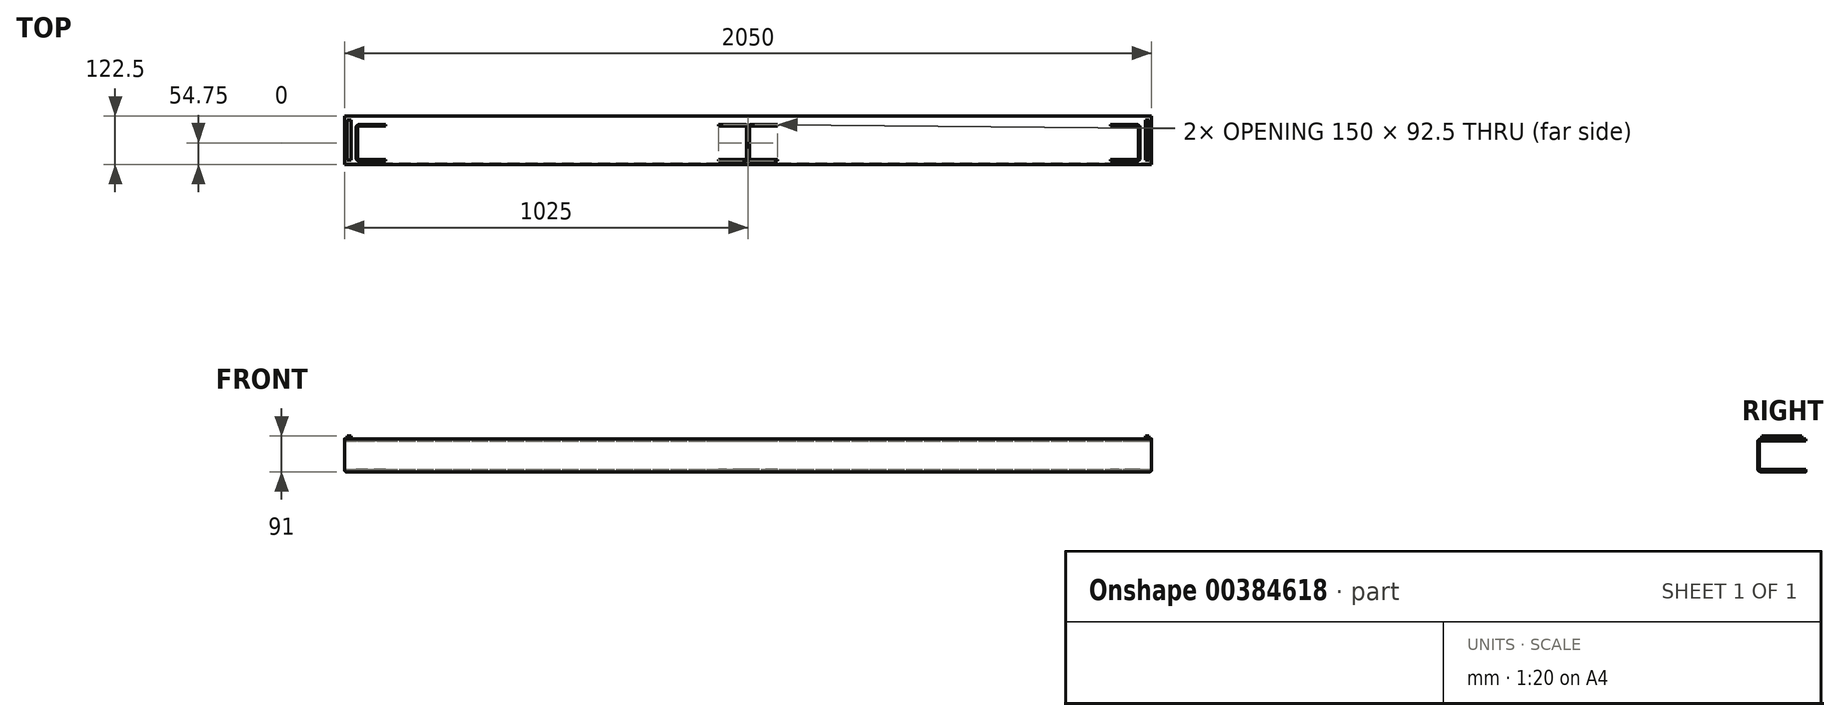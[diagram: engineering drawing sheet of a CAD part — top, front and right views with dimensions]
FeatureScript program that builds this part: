
annotation { "Feature Type Name" : "Feature", "Feature Type Description" : "" }
export const myFeature = defineFeature(function(context is Context, id is Id, definition is map)
    precondition{}
    {
        {
            var Q0;
            Q0=qCreatedBy(makeId("Right.planeOp"),FACE);
            var sketch = newSketch(context, id + "F0", { "sketchPlane" : qUnion([Q0])});
            skLineSegment(sketch, "E0.bottom", {"start": v(-45.5, -41.75) * mm, "end": v(0, -41.75) * mm});
            skLineSegment(sketch, "E0.top", {"start": v(-45.5, 41.75) * mm, "end": v(0, 41.75) * mm});
            skLineSegment(sketch, "E0.left", {"start": v(-53.5, -33.75) * mm, "end": v(-53.5, 33.75) * mm});
            skPoint(sketch, "E0.middle", {"position": v(0, 0) * mm});
            skLineSegment(sketch, "E1", {"start": v(0, 36) * mm, "end": v(-45.5, 36) * mm});
            skLineSegment(sketch, "E2", {"start": v(-49.5, 32) * mm, "end": v(-49.5, -32) * mm});
            skLineSegment(sketch, "E3", {"start": v(-45.5, -36) * mm, "end": v(0, -36) * mm});
            skPoint(sketch, "E4.visualSharp", {"position": v(-49.5, 36) * mm});
            skArc(sketch, "E4.filletArc", {"start": v(-45.5, 36) * mm, "mid": v(-48.33, 34.83) * mm, "end": v(-49.5, 32) * mm});
            skPoint(sketch, "E5.visualSharp", {"position": v(-49.5, -36) * mm});
            skArc(sketch, "E5.filletArc", {"start": v(-49.5, -32) * mm, "mid": v(-48.33, -34.83) * mm, "end": v(-45.5, -36) * mm});
            skPoint(sketch, "E6.visualSharp", {"position": v(-53.5, 41.75) * mm});
            skArc(sketch, "E6.filletArc", {"start": v(-45.5, 41.75) * mm, "mid": v(-51.16, 39.4) * mm, "end": v(-53.5, 33.75) * mm});
            skPoint(sketch, "E7.visualSharp", {"position": v(-53.5, -41.75) * mm});
            skArc(sketch, "E7.filletArc", {"start": v(-53.5, -33.75) * mm, "mid": v(-51.16, -39.4) * mm, "end": v(-45.5, -41.75) * mm});
            skLineSegment(sketch, "E8", {"start": v(0, 41.75) * mm, "end": v(0, -41.75) * mm});
            skPoint(sketch, "E8.startSnap0", {"position": v(4, 41.75) * mm});
            skPoint(sketch, "E9.start.orphan", {"position": v(53.5, 41.75) * mm});
            skPoint(sketch, "E0.right.start.orphan", {"position": v(53.5, -41.75) * mm});
            skLineSegment(sketch, "E10", {"start": v(0, 41.75) * mm, "end": v(69, 41.75) * mm});
            skLineSegment(sketch, "E11", {"start": v(69, 41.75) * mm, "end": v(69, 36) * mm});
            skLineSegment(sketch, "E12", {"start": v(0, -41.75) * mm, "end": v(69, -41.75) * mm});
            skLineSegment(sketch, "E13", {"start": v(69, -41.75) * mm, "end": v(69, -36) * mm});
            skLineSegment(sketch, "E14", {"start": v(69, -36) * mm, "end": v(0, -36) * mm});
            skLineSegment(sketch, "E15", {"start": v(69, 36) * mm, "end": v(0, 36) * mm});
            skSolve(sketch);
        }
        {
            var Q0;
            Q0=makeQuery(id+"F0.imprint","IMPRINT",FACE,{"disambiguationData":[TD([[makeQuery(id+"F0.imprint","IMPRINT",EDGE,{"derivedFrom":sQuery(id+"F0.wireOp",EDGE,"E0.bottom")}),1.0]])]});
            var Q1;
            {var subQ0=sQuery(id+"F0.wireOp",EDGE,"E10");Q1=makeQuery(id+"F0.imprint","IMPRINT",FACE,{"disambiguationData":[TD([[makeQuery(id+"F0.imprint","IMPRINT",EDGE,{"derivedFrom":subQ0}),-1.0]])]});}
            var Q2;
            {var subQ0=sQuery(id+"F0.wireOp",EDGE,"E12");Q2=makeQuery(id+"F0.imprint","IMPRINT",FACE,{"disambiguationData":[TD([[makeQuery(id+"F0.imprint","IMPRINT",EDGE,{"derivedFrom":subQ0}),1.0]])]});}
            extrude(context, id + "F1", {"entities" : qUnion([Q0, Q1, Q2]), "oppositeDirection" : true, "depth" : 2050 * mm});
        }
        {
            var Q0;
            Q0=makeQuery(id+"F1.opExtrude","SWEPT_FACE",FACE,{"disambiguationData":[OSD([sQuery(id+"F0.wireOp",EDGE,"E0.top")])]});
            var sketch = newSketch(context, id + "F2", { "sketchPlane" : qUnion([Q0])});
            skLineSegment(sketch, "E16", {"start": v(-2044, 59) * mm, "end": v(-2044, -42.5) * mm});
            skLineSegment(sketch, "E17", {"start": v(-2044, -42.5) * mm, "end": v(-2034, -42.5) * mm});
            skLineSegment(sketch, "E18", {"start": v(-2034, -42.5) * mm, "end": v(-2034, 59) * mm});
            skLineSegment(sketch, "E19", {"start": v(-2034, 59) * mm, "end": v(-2044, 59) * mm});
            skPoint(sketch, "E20.end.orphan", {"position": v(-2044, -45.5) * mm});
            skCircle(sketch, "E21", {"center": v(-15, -15.03) * mm, "radius": 8.13 * mm});
            skCircle(sketch, "E22", {"center": v(15, 15.03) * mm, "radius": 8.06 * mm});
            skSolve(sketch);
        }
        {
            var Q0;
            Q0=makeQuery(id+"F2.imprint","IMPRINT",FACE,{"disambiguationData":[TD([[makeQuery(id+"F2.imprint","IMPRINT",EDGE,{"derivedFrom":sQuery(id+"F2.wireOp",EDGE,"E16")}),1.0]])]});
            extrude(context, id + "F3", {"entities" : qUnion([Q0]), "operationType" : NewBodyOperationType.ADD, "depth" : 7.5 * mm});
        }
        {
            var Q0;
            Q0=qCreatedBy(makeId("Right.planeOp"),FACE);
            cPlane(context, id + "F4", {"entities" : qUnion([Q0]), "cplaneType" : CPlaneType.OFFSET, "offset" : 1025 * mm, "oppositeDirection" : true, "width" : 150 * mm, "height" : 150 * mm});
        }
        {
            var Q0;
            Q0=makeQuery(id+"F1.opExtrude","SWEPT_BODY",BODY,{"disambiguationData":[OSD([sQuery(id+"F0.wireOp",EDGE,"E0.bottom"),sQuery(id+"F0.wireOp",EDGE,"E0.top"),sQuery(id+"F0.wireOp",EDGE,"E0.left"),sQuery(id+"F0.wireOp",EDGE,"E0.right"),sQuery(id+"F0.wireOp",EDGE,"E1"),sQuery(id+"F0.wireOp",EDGE,"E2"),sQuery(id+"F0.wireOp",EDGE,"E3"),sQuery(id+"F0.wireOp",EDGE,"f9d5d635-1330-4c21-9b24-47b6535b446e.trimOffspring"),sQuery(id+"F0.wireOp",EDGE,"E4.filletArc"),sQuery(id+"F0.wireOp",EDGE,"E5.filletArc"),sQuery(id+"F0.wireOp",EDGE,"E6.filletArc"),sQuery(id+"F0.wireOp",EDGE,"E7.filletArc")])]});
            var Q1;
            Q1=qCreatedBy(id+"F4.planeOp",FACE);
            mirror(context, id + "F5", {"operationType" : NewBodyOperationType.ADD, "entities" : qUnion([Q0]), "mirrorPlane" : qUnion([Q1])});
        }
        {
            var Q0;
            Q0=makeQuery(id+"F2.imprint","IMPRINT",FACE,{"disambiguationData":[TD([[makeQuery(id+"F2.imprint","IMPRINT",EDGE,{"derivedFrom":sQuery(id+"F2.wireOp",EDGE,"E16")}),-1.0]])]});
            var sketch = newSketch(context, id + "F6", { "sketchPlane" : qUnion([Q0])});
            skLineSegment(sketch, "E23", {"start": v(-2021, 0) * mm, "end": v(-2021, 39.5) * mm});
            skLineSegment(sketch, "E24", {"start": v(-2013, 47.5) * mm, "end": v(-1945.5, 47.5) * mm});
            skLineSegment(sketch, "E25", {"start": v(-1945.5, 47.5) * mm, "end": v(-1945.5, 43.25) * mm});
            skLineSegment(sketch, "E26", {"start": v(-1945.5, -41.25) * mm, "end": v(-1945.5, -45.5) * mm});
            skLineSegment(sketch, "E27", {"start": v(-1945.5, -45.5) * mm, "end": v(-2013, -45.5) * mm});
            skLineSegment(sketch, "E28", {"start": v(-2021, -37.5) * mm, "end": v(-2021, 0) * mm});
            skPoint(sketch, "E29.visualSharp", {"position": v(-1992.5, 39) * mm});
            skPoint(sketch, "E30.visualSharp", {"position": v(-2021, 47.5) * mm});
            skArc(sketch, "E30.filletArc", {"start": v(-2013, 47.5) * mm, "mid": v(-2018.66, 45.16) * mm, "end": v(-2021, 39.5) * mm});
            skPoint(sketch, "E31.visualSharp", {"position": v(-2021, -45.5) * mm});
            skArc(sketch, "E31.filletArc", {"start": v(-2021, -37.5) * mm, "mid": v(-2018.66, -43.16) * mm, "end": v(-2013, -45.5) * mm});
            skLineSegment(sketch, "E32", {"start": v(-1945.5, 43.25) * mm, "end": v(-2012.75, 43.25) * mm});
            skPoint(sketch, "E32.endSnap0", {"position": v(-2018.66, 45.16) * mm});
            skPoint(sketch, "E33.endSnap0", {"position": v(-1945.5, -43.38) * mm});
            skPoint(sketch, "E34.start.orphan", {"position": v(-1945.5, 39) * mm});
            skLineSegment(sketch, "E35", {"start": v(-2004.97, -41.25) * mm, "end": v(-2004.97, -43.16) * mm});
            skPoint(sketch, "E36.orphan", {"position": v(-2018.66, -43.16) * mm});
            skPoint(sketch, "E33.end.orphan", {"position": v(-1945.5, -43.16) * mm});
            skLineSegment(sketch, "E37", {"start": v(-1945.5, -41.25) * mm, "end": v(-2012.75, -41.25) * mm});
            skLineSegment(sketch, "E38.0", {"start": v(-2016.75, 0) * mm, "end": v(-2016.75, 39.25) * mm});
            skLineSegment(sketch, "E38.1", {"start": v(-2016.75, -37.25) * mm, "end": v(-2016.75, 0) * mm});
            skArc(sketch, "E39.filletArc", {"start": v(-2016.75, -37.25) * mm, "mid": v(-2015.58, -40.08) * mm, "end": v(-2012.75, -41.25) * mm});
            skPoint(sketch, "E40.newPointB", {"position": v(-2018.66, 43.25) * mm});
            skArc(sketch, "E40.filletArc", {"start": v(-2012.75, 43.25) * mm, "mid": v(-2015.58, 42.08) * mm, "end": v(-2016.75, 39.25) * mm});
            skSolve(sketch);
        }
        {
            var Q0;
            Q0=makeQuery(id+"F6.imprint","IMPRINT",FACE,{"disambiguationData":[TD([[makeQuery(id+"F6.imprint","IMPRINT",EDGE,{"derivedFrom":sQuery(id+"F6.wireOp",EDGE,"E23")}),-1.0]])]});
            extrude(context, id + "F7", {"entities" : qUnion([Q0]), "operationType" : NewBodyOperationType.REMOVE, "oppositeDirection" : true, "depth" : 84 * mm});
        }
        {
            var Q0;
            Q0=makeQuery(id+"F1.opExtrude","SWEPT_BODY",BODY,{"disambiguationData":[OSD([sQuery(id+"F0.wireOp",EDGE,"E0.bottom"),sQuery(id+"F0.wireOp",EDGE,"E0.top"),sQuery(id+"F0.wireOp",EDGE,"E0.left"),sQuery(id+"F0.wireOp",EDGE,"E0.right"),sQuery(id+"F0.wireOp",EDGE,"E1"),sQuery(id+"F0.wireOp",EDGE,"E2"),sQuery(id+"F0.wireOp",EDGE,"E3"),sQuery(id+"F0.wireOp",EDGE,"f9d5d635-1330-4c21-9b24-47b6535b446e.trimOffspring"),sQuery(id+"F0.wireOp",EDGE,"E4.filletArc"),sQuery(id+"F0.wireOp",EDGE,"E5.filletArc"),sQuery(id+"F0.wireOp",EDGE,"E6.filletArc"),sQuery(id+"F0.wireOp",EDGE,"E7.filletArc")])]});
            var Q1;
            Q1=qCreatedBy(id+"F4.planeOp",FACE);
            mirror(context, id + "F8", {"operationType" : NewBodyOperationType.INTERSECT, "entities" : qUnion([Q0]), "mirrorPlane" : qUnion([Q1])});
        }
        {
            var Q0;
            Q0=makeQuery(id+"F6.imprint","IMPRINT",FACE,{"disambiguationData":[TD([[makeQuery(id+"F6.imprint","IMPRINT",EDGE,{"derivedFrom":sQuery(id+"F6.wireOp",EDGE,"E23")}),1.0]])]});
            var sketch = newSketch(context, id + "F9", { "sketchPlane" : qUnion([Q0])});
            skLineSegment(sketch, "E41.bottom", {"start": v(-1017, -45) * mm, "end": v(-950, -45) * mm});
            skLineSegment(sketch, "E41.top", {"start": v(-1100, 47.5) * mm, "end": v(-1033, 47.5) * mm});
            skLineSegment(sketch, "E41.left", {"start": v(-1100, -45) * mm, "end": v(-1100, -40.75) * mm});
            skLineSegment(sketch, "E41.right", {"start": v(-950, -45) * mm, "end": v(-950, -40.75) * mm});
            skPoint(sketch, "E41.middle", {"position": v(-1025, 1.25) * mm});
            skLineSegment(sketch, "E42.bottom", {"start": v(-1100, -40.75) * mm, "end": v(-1033.25, -40.75) * mm});
            skLineSegment(sketch, "E42.top", {"start": v(-1100, 43.25) * mm, "end": v(-1033.25, 43.25) * mm});
            skLineSegment(sketch, "E43", {"start": v(-1029.25, 1.25) * mm, "end": v(-1029.25, 39.25) * mm});
            skLineSegment(sketch, "E44", {"start": v(-1029.25, 1.25) * mm, "end": v(-1029.25, -36.75) * mm});
            skLineSegment(sketch, "E45", {"start": v(-1020.75, 1.25) * mm, "end": v(-1020.75, 39.25) * mm});
            skLineSegment(sketch, "E46", {"start": v(-1020.75, 1.25) * mm, "end": v(-1020.75, -36.75) * mm});
            skLineSegment(sketch, "E47.trimOffspring", {"start": v(-1016.75, 43.25) * mm, "end": v(-950, 43.25) * mm});
            skLineSegment(sketch, "E48.trimOffspring", {"start": v(-1016.75, -40.75) * mm, "end": v(-950, -40.75) * mm});
            skPoint(sketch, "E42.left.end.orphan", {"position": v(-1095.75, 43.25) * mm});
            skPoint(sketch, "E42.left.start.orphan", {"position": v(-1095.75, -40.75) * mm});
            skLineSegment(sketch, "E49.trimOffspring", {"start": v(-1100, 43.25) * mm, "end": v(-1100, 47.5) * mm});
            skLineSegment(sketch, "E50.trimOffspring", {"start": v(-950, 43.25) * mm, "end": v(-950, 47.5) * mm});
            skPoint(sketch, "E42.right.end.orphan", {"position": v(-954.25, 43.25) * mm});
            skPoint(sketch, "E42.right.start.orphan", {"position": v(-954.25, -40.75) * mm});
            skPoint(sketch, "E51.newPointA", {"position": v(-950, 47.5) * mm});
            skPoint(sketch, "E51.newPointB", {"position": v(-1025, 47.5) * mm});
            skArc(sketch, "E51.filletArc", {"start": v(-1025.93, 43.25) * mm, "mid": v(-1028.88, 46.36) * mm, "end": v(-1033, 47.5) * mm});
            skLineSegment(sketch, "E52", {"start": v(-1025, 39.5) * mm, "end": v(-1025, 39.5) * mm});
            skLineSegment(sketch, "E53", {"start": v(-1017, 47.5) * mm, "end": v(-950, 47.5) * mm});
            skArc(sketch, "E54.filletArc", {"start": v(-1017, 47.5) * mm, "mid": v(-1021.12, 46.36) * mm, "end": v(-1024.07, 43.25) * mm});
            skPoint(sketch, "E55.newPointA", {"position": v(-1025, -45) * mm});
            skPoint(sketch, "E55.newPointB", {"position": v(-1100, -45) * mm});
            skArc(sketch, "E55.filletArc", {"start": v(-1024.07, -40.75) * mm, "mid": v(-1021.12, -43.86) * mm, "end": v(-1017, -45) * mm});
            skLineSegment(sketch, "E56", {"start": v(-1025, -37) * mm, "end": v(-1025, -37) * mm});
            skLineSegment(sketch, "E57", {"start": v(-1033, -45) * mm, "end": v(-1100, -45) * mm});
            skArc(sketch, "E58.filletArc", {"start": v(-1033, -45) * mm, "mid": v(-1028.88, -43.86) * mm, "end": v(-1025.93, -40.75) * mm});
            skPoint(sketch, "E59.visualSharp", {"position": v(-1029.25, 43.25) * mm});
            skArc(sketch, "E59.filletArc", {"start": v(-1029.25, 39.25) * mm, "mid": v(-1030.42, 42.08) * mm, "end": v(-1033.25, 43.25) * mm});
            skPoint(sketch, "E60.visualSharp", {"position": v(-1020.75, 43.25) * mm});
            skArc(sketch, "E60.filletArc", {"start": v(-1016.75, 43.25) * mm, "mid": v(-1019.58, 42.08) * mm, "end": v(-1020.75, 39.25) * mm});
            skPoint(sketch, "E61.visualSharp", {"position": v(-1020.75, -40.75) * mm});
            skArc(sketch, "E61.filletArc", {"start": v(-1020.75, -36.75) * mm, "mid": v(-1019.58, -39.58) * mm, "end": v(-1016.75, -40.75) * mm});
            skPoint(sketch, "E62.visualSharp", {"position": v(-1029.25, -40.75) * mm});
            skArc(sketch, "E62.filletArc", {"start": v(-1033.25, -40.75) * mm, "mid": v(-1030.42, -39.58) * mm, "end": v(-1029.25, -36.75) * mm});
            skLineSegment(sketch, "E63", {"start": v(-1025.93, 43.25) * mm, "end": v(-1024.07, 43.25) * mm});
            skLineSegment(sketch, "E64", {"start": v(-1025.93, -40.75) * mm, "end": v(-1024.07, -40.75) * mm});
            skSolve(sketch);
        }
        {
            var Q0;
            Q0=makeQuery(id+"F9.imprint","IMPRINT",FACE,{"disambiguationData":[TD([[makeQuery(id+"F9.imprint","IMPRINT",EDGE,{"derivedFrom":sQuery(id+"F9.wireOp",EDGE,"E41.bottom")}),1.0]])]});
            extrude(context, id + "F10", {"entities" : qUnion([Q0]), "operationType" : NewBodyOperationType.REMOVE, "oppositeDirection" : true, "depth" : 90 * mm});
        }
        {
            var Q0;
            Q0=makeQuery(id+"F1.opExtrude","CAP_EDGE",EDGE,{"disambiguationData":[OSD([sQuery(id+"F0.wireOp",EDGE,"E0.bottom")])],"isStart":false});
            fillet(context, id + "F11", {"entities" : qUnion([Q0]), "radius" : 4 * mm, "allowEdgeOverflow" : false});
        }
        {
            var Q0;
            Q0=makeQuery(id+"F1.opExtrude","CAP_EDGE",EDGE,{"disambiguationData":[OSD([sQuery(id+"F0.wireOp",EDGE,"E0.bottom")])],"isStart":true});
            fillet(context, id + "F12", {"entities" : qUnion([Q0]), "radius" : 5 * mm, "allowEdgeOverflow" : false});
        }
    });
